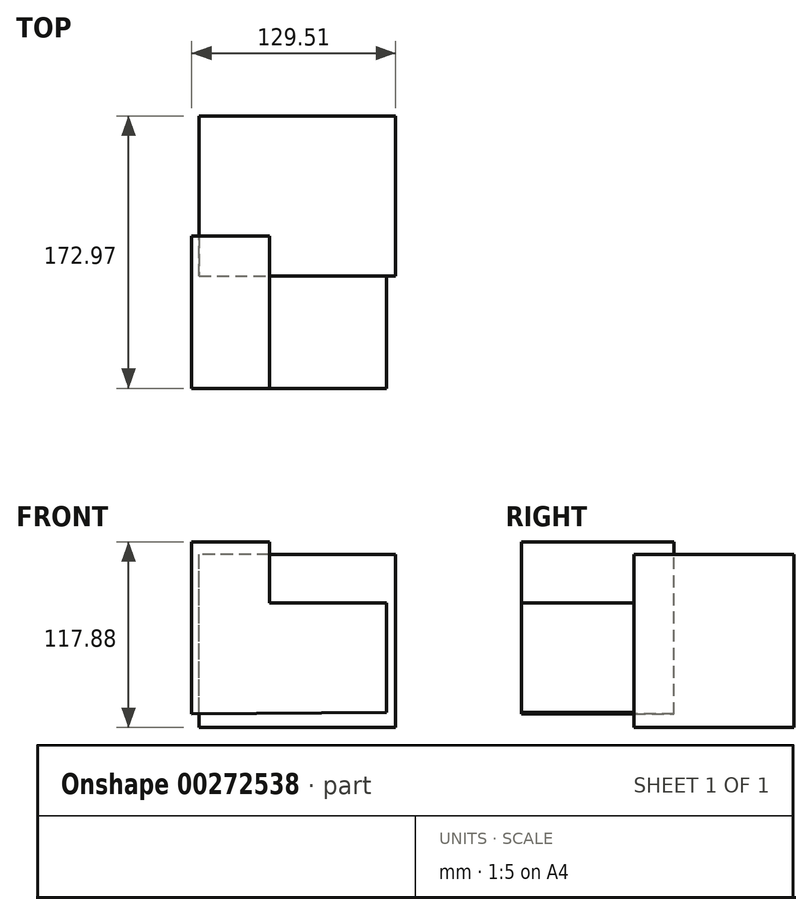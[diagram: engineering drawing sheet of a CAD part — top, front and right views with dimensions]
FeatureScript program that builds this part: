
annotation { "Feature Type Name" : "Feature", "Feature Type Description" : "" }
export const myFeature = defineFeature(function(context is Context, id is Id, definition is map)
    precondition{}
    {
        {
            var Q0;
            Q0=qCreatedBy(makeId("Front.planeOp"),FACE);
            var sketch = newSketch(context, id + "F0", { "sketchPlane" : qUnion([Q0])});
            skLineSegment(sketch, "E0.bottom", {"start": v(0, 0) * mm, "end": v(-62.54, 0) * mm});
            skLineSegment(sketch, "E0.top", {"start": v(0, 53.09) * mm, "end": v(-62.54, 53.09) * mm});
            skLineSegment(sketch, "E0.left", {"start": v(0, 0) * mm, "end": v(0, 53.09) * mm});
            skLineSegment(sketch, "E0.right", {"start": v(-62.54, 0) * mm, "end": v(-62.54, 53.09) * mm});
            skLineSegment(sketch, "E1.bottom", {"start": v(0, 53.09) * mm, "end": v(62.16, 53.09) * mm});
            skLineSegment(sketch, "E1.top", {"start": v(0, 0) * mm, "end": v(62.16, 0) * mm});
            skLineSegment(sketch, "E1.left", {"start": v(0, 53.09) * mm, "end": v(0, 0) * mm});
            skLineSegment(sketch, "E1.right", {"start": v(62.16, 53.09) * mm, "end": v(62.16, 0) * mm});
            skLineSegment(sketch, "E2.bottom", {"start": v(-62.54, 0) * mm, "end": v(62.16, 0) * mm});
            skLineSegment(sketch, "E2.top", {"start": v(-62.54, -56.9) * mm, "end": v(62.16, -56.9) * mm});
            skLineSegment(sketch, "E2.left", {"start": v(-62.54, 0) * mm, "end": v(-62.54, -56.9) * mm});
            skLineSegment(sketch, "E2.right", {"start": v(62.16, 0) * mm, "end": v(62.16, -56.9) * mm});
            skSolve(sketch);
        }
        {
            var Q0;
            Q0 = qSketchRegion(id + "F0", true);
            extrude(context, id + "F1", {"entities" : qUnion([Q0]), "depth" : 25.4 * mm});
        }
        {
            var Q0;
            Q0 = qSketchRegion(id + "F0", true);
            extrude(context, id + "F2", {"entities" : qUnion([Q0]), "operationType" : NewBodyOperationType.ADD, "oppositeDirection" : true, "depth" : 76.2 * mm});
        }
        {
            var Q0;
            Q0=qCreatedBy(makeId("Front.planeOp"),FACE);
            var sketch = newSketch(context, id + "F3", { "sketchPlane" : qUnion([Q0])});
            skLineSegment(sketch, "E3", {"start": v(-67.35, -48.38) * mm, "end": v(-67.35, 60.98) * mm});
            skLineSegment(sketch, "E4", {"start": v(-67.35, 60.98) * mm, "end": v(-18, 60.98) * mm});
            skLineSegment(sketch, "E5", {"start": v(-18, 60.98) * mm, "end": v(-18, 22.28) * mm});
            skLineSegment(sketch, "E6", {"start": v(-18, 22.28) * mm, "end": v(56.29, 22.28) * mm});
            skLineSegment(sketch, "E7", {"start": v(56.29, 22.28) * mm, "end": v(56.29, -47.44) * mm});
            skLineSegment(sketch, "E8", {"start": v(56.29, -47.44) * mm, "end": v(-67.35, -48.38) * mm});
            skSolve(sketch);
        }
        {
            var Q0;
            Q0 = qSketchRegion(id + "F3", true);
            extrude(context, id + "F4", {"entities" : qUnion([Q0]), "operationType" : NewBodyOperationType.ADD, "depth" : 96.77 * mm});
        }
    });
